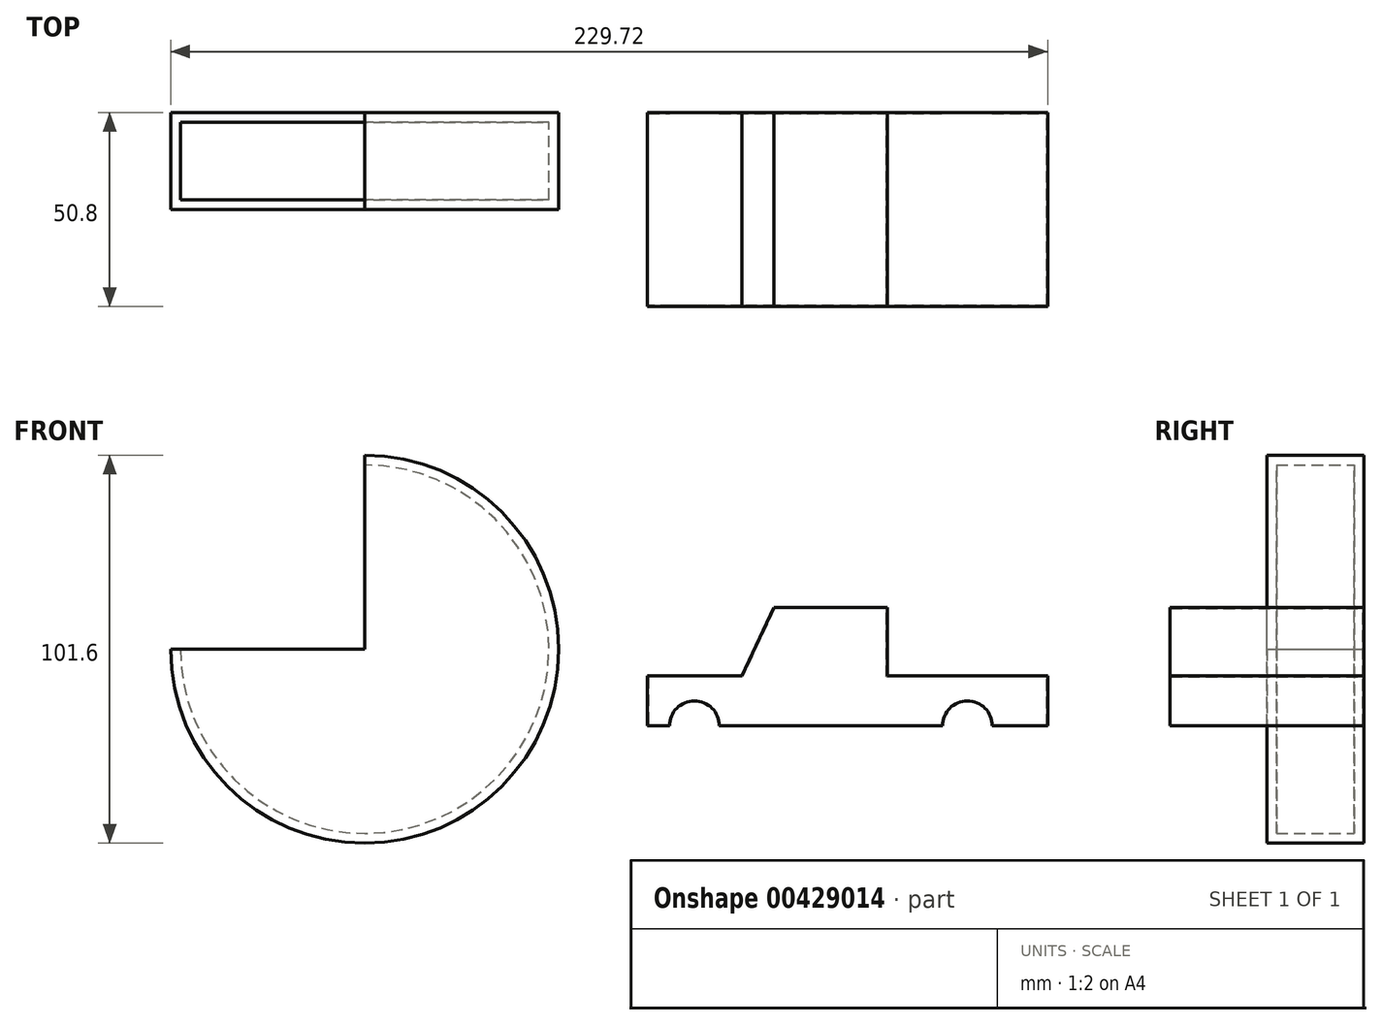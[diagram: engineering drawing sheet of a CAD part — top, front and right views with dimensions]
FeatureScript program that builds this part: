
annotation { "Feature Type Name" : "Feature", "Feature Type Description" : "" }
export const myFeature = defineFeature(function(context is Context, id is Id, definition is map)
    precondition{}
    {
        {
            var Q0;
            Q0=qCreatedBy(makeId("Front.planeOp"),FACE);
            var sketch = newSketch(context, id + "F0", { "sketchPlane" : qUnion([Q0])});
            skCircle(sketch, "E0", {"center": v(-35.92, 35.92) * mm, "radius": 50.8 * mm});
            skLineSegment(sketch, "E1", {"start": v(-22.76, 0) * mm, "end": v(0, 0) * mm});
            skLineSegment(sketch, "E2", {"start": v(0, 0) * mm, "end": v(-35.92, 35.92) * mm});
            skSolve(sketch);
        }
        {
            var Q0;
            Q0=makeQuery(id+"F0.imprint","IMPRINT",FACE,{"disambiguationData":[TD([[makeQuery(id+"F0.imprint","IMPRINT",EDGE,{"derivedFrom":sQuery(id+"F0.wireOp",EDGE,"E0")}),1.0]])]});
            extrude(context, id + "F1", {"entities" : qUnion([Q0]), "depth" : 25.4 * mm});
        }
        {
            var Q0;
            Q0=makeQuery(id+"F1.opExtrude","CAP_FACE",FACE,{"disambiguationData":[OSD([sQuery(id+"F0.wireOp",EDGE,"E0")])],"isStart":false});
            var Q1;
            Q1=makeQuery(id+"F1.opExtrude","SWEPT_BODY",BODY,{"disambiguationData":[OSD([sQuery(id+"F0.wireOp",EDGE,"E0")])]});
            shell(context, id + "F2", {"isHollow" : true, "entities" : qUnion([Q0]), "parts" : qUnion([Q1]), "thickness" : 2.54 * mm});
        }
        {
            var Q0;
            Q0=makeQuery(id+"F1.opExtrude","CAP_FACE",FACE,{"disambiguationData":[OSD([sQuery(id+"F0.wireOp",EDGE,"E0")])],"isStart":true});
            var sketch = newSketch(context, id + "F3", { "sketchPlane" : qUnion([Q0])});
            skLineSegment(sketch, "E3", {"start": v(35.92, 35.92) * mm, "end": v(35.92, 86.72) * mm});
            skLineSegment(sketch, "E4", {"start": v(35.92, 35.92) * mm, "end": v(86.72, 35.92) * mm});
            skSolve(sketch);
        }
        {
            var Q0;
            {var subQ0=sQuery(id+"F3.wireOp",EDGE,"E3");Q0=makeQuery(id+"F3.imprint","IMPRINT",FACE,{"disambiguationData":[TD([[makeQuery(id+"F3.imprint","IMPRINT",EDGE,{"derivedFrom":subQ0}),-1.0]])]});}
            extrude(context, id + "F4", {"entities" : qUnion([Q0]), "operationType" : NewBodyOperationType.REMOVE, "oppositeDirection" : true, "depth" : 25.4 * mm});
        }
        {
            var Q0;
            Q0=qCreatedBy(makeId("Front.planeOp"),FACE);
            var sketch = newSketch(context, id + "F5", { "sketchPlane" : qUnion([Q0])});
            skLineSegment(sketch, "E5", {"start": v(143, 28.88) * mm, "end": v(100.96, 28.88) * mm});
            skLineSegment(sketch, "E6", {"start": v(100.96, 28.88) * mm, "end": v(100.96, 46.8) * mm});
            skLineSegment(sketch, "E7", {"start": v(100.96, 46.8) * mm, "end": v(71.31, 46.8) * mm});
            skLineSegment(sketch, "E8", {"start": v(71.31, 46.8) * mm, "end": v(62.84, 28.88) * mm});
            skLineSegment(sketch, "E9", {"start": v(62.84, 28.88) * mm, "end": v(38.08, 28.88) * mm});
            skLineSegment(sketch, "E10", {"start": v(38.08, 28.88) * mm, "end": v(38.08, 15.85) * mm});
            skLineSegment(sketch, "E11", {"start": v(38.08, 15.85) * mm, "end": v(43.94, 15.85) * mm});
            skLineSegment(sketch, "E12", {"start": v(62.84, 15.85) * mm, "end": v(100.96, 15.85) * mm});
            skLineSegment(sketch, "E13", {"start": v(100.96, 15.85) * mm, "end": v(115.46, 15.85) * mm});
            skLineSegment(sketch, "E14", {"start": v(143, 15.85) * mm, "end": v(143, 28.88) * mm});
            skCircle(sketch, "E15", {"center": v(121.98, 15.85) * mm, "radius": 6.52 * mm});
            skLineSegment(sketch, "E16.trimOffspring", {"start": v(128.5, 15.85) * mm, "end": v(143, 15.85) * mm});
            skCircle(sketch, "E17", {"center": v(50.46, 15.85) * mm, "radius": 6.52 * mm});
            skLineSegment(sketch, "E18.trimOffspring", {"start": v(56.98, 15.85) * mm, "end": v(62.84, 15.85) * mm});
            skSolve(sketch);
        }
        {
            var Q0;
            Q0=makeQuery(id+"F5.imprint","IMPRINT",FACE,{"disambiguationData":[TD([[makeQuery(id+"F5.imprint","IMPRINT",EDGE,{"derivedFrom":sQuery(id+"F5.wireOp",EDGE,"E5")}),1.0]])]});
            extrude(context, id + "F6", {"entities" : qUnion([Q0]), "depth" : 50.8 * mm});
        }
        {
            var Q0;
            Q0=makeQuery(id+"F6.opExtrude","SWEPT_FACE",FACE,{"disambiguationData":[OSD([sQuery(id+"F5.wireOp",EDGE,"E12"),sQuery(id+"F5.wireOp",EDGE,"E13"),sQuery(id+"F5.wireOp",EDGE,"E18.trimOffspring")])]});
            var Q1;
            Q1=makeQuery(id+"F6.opExtrude","SWEPT_FACE",FACE,{"disambiguationData":[OSD([sQuery(id+"F5.wireOp",EDGE,"E16.trimOffspring")])]});
            var Q2;
            Q2=makeQuery(id+"F6.opExtrude","SWEPT_FACE",FACE,{"disambiguationData":[OSD([sQuery(id+"F5.wireOp",EDGE,"E15")])]});
            var Q3;
            Q3=makeQuery(id+"F6.opExtrude","SWEPT_FACE",FACE,{"disambiguationData":[OSD([sQuery(id+"F5.wireOp",EDGE,"E17")])]});
            var Q4;
            Q4=makeQuery(id+"F6.opExtrude","SWEPT_FACE",FACE,{"disambiguationData":[OSD([sQuery(id+"F5.wireOp",EDGE,"E11")])]});
            shell(context, id + "F7", {"entities" : qUnion([Q0, Q1, Q2, Q3, Q4]), "thickness" : 0.25 * mm});
        }
    });
